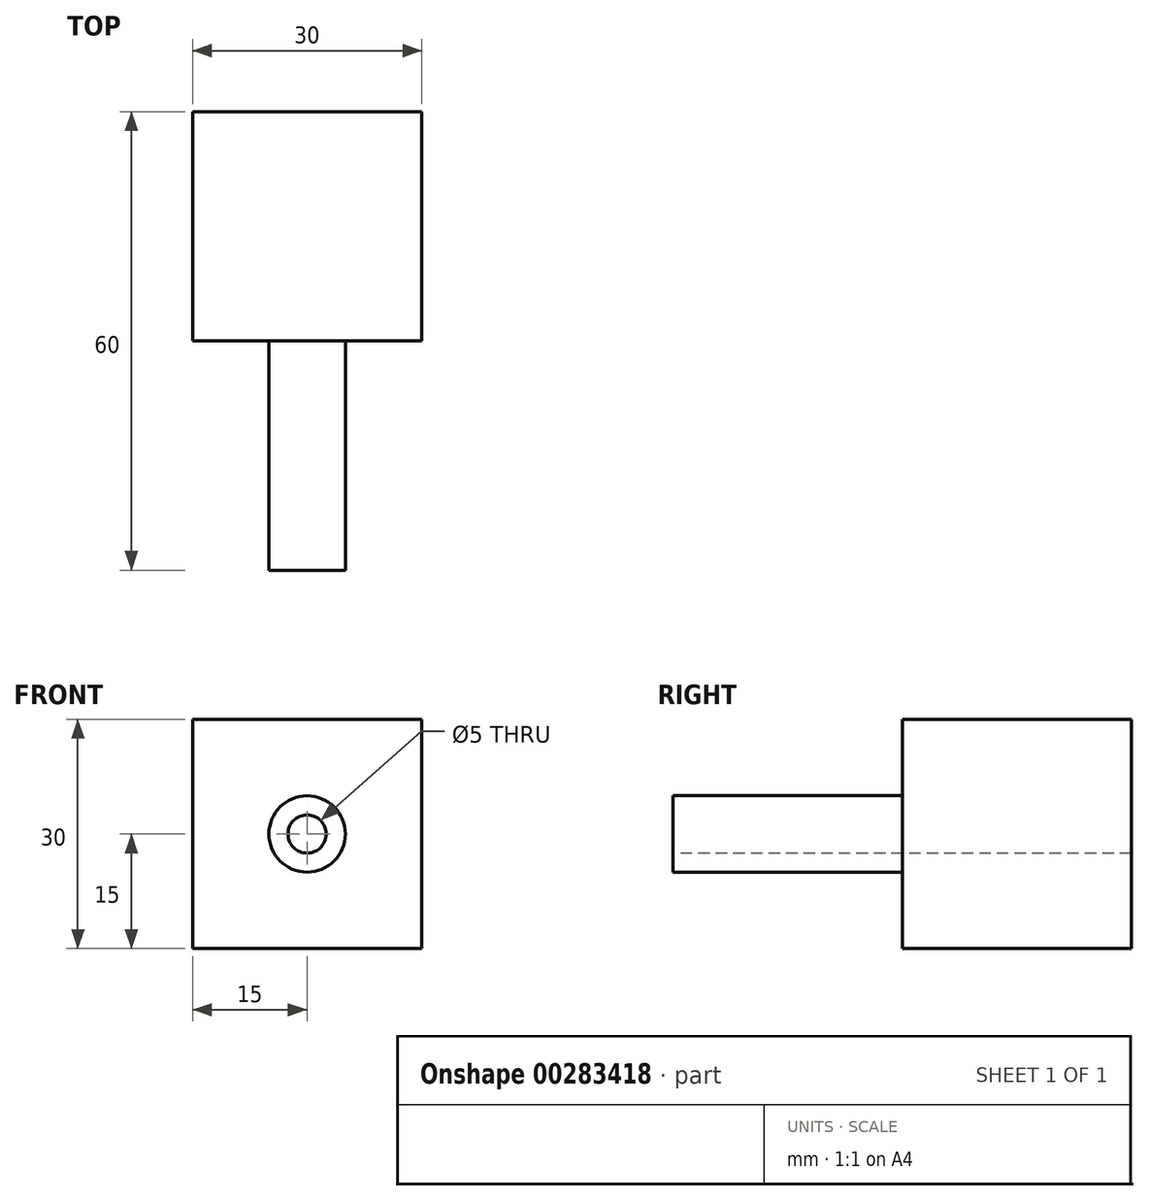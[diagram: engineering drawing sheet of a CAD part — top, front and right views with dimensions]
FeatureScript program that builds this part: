
annotation { "Feature Type Name" : "Feature", "Feature Type Description" : "" }
export const myFeature = defineFeature(function(context is Context, id is Id, definition is map)
    precondition{}
    {
        {
            var Q0;
            Q0=qCreatedBy(makeId("Top.planeOp"),FACE);
            var sketch = newSketch(context, id + "F0", { "sketchPlane" : qUnion([Q0])});
            skLineSegment(sketch, "E0.bottom", {"start": v(-15, 15) * mm, "end": v(15, 15) * mm});
            skLineSegment(sketch, "E0.top", {"start": v(-15, -15) * mm, "end": v(15, -15) * mm});
            skLineSegment(sketch, "E0.left", {"start": v(-15, 15) * mm, "end": v(-15, -15) * mm});
            skLineSegment(sketch, "E0.right", {"start": v(15, 15) * mm, "end": v(15, -15) * mm});
            skPoint(sketch, "E0.middle", {"position": v(0, 0) * mm});
            skSolve(sketch);
        }
        {
            var Q0;
            Q0=makeQuery(id+"F0.imprint","IMPRINT",FACE,{"disambiguationData":[TD([[makeQuery(id+"F0.imprint","IMPRINT",EDGE,{"derivedFrom":sQuery(id+"F0.wireOp",EDGE,"E0.bottom")}),-1.0]])]});
            extrude(context, id + "F1", {"entities" : qUnion([Q0]), "endBound" : BoundingType.SYMMETRIC, "depth" : 30 * mm});
        }
        {
            var Q0;
            Q0=makeQuery(id+"F1.opExtrude","SWEPT_FACE",FACE,{"disambiguationData":[OSD([sQuery(id+"F0.wireOp",EDGE,"E0.top")])]});
            var sketch = newSketch(context, id + "F2", { "sketchPlane" : qUnion([Q0])});
            skCircle(sketch, "E1", {"center": v(0, 0) * mm, "radius": 5 * mm});
            skSolve(sketch);
        }
        {
            var Q0;
            Q0 = qSketchRegion(id + "F2", true);
            extrude(context, id + "F3", {"entities" : qUnion([Q0]), "operationType" : NewBodyOperationType.ADD, "depth" : 30 * mm});
        }
        {
            var Q0;
            Q0=makeQuery(id+"F3.opExtrude","CAP_FACE",FACE,{"disambiguationData":[OSD([sQuery(id+"F2.wireOp",EDGE,"E1")])],"isStart":false});
            var sketch = newSketch(context, id + "F4", { "sketchPlane" : qUnion([Q0])});
            skCircle(sketch, "E2", {"center": v(0, 0) * mm, "radius": 2.5 * mm});
            skSolve(sketch);
        }
        {
            var Q0;
            Q0=makeQuery(id+"F4.imprint","IMPRINT",FACE,{"disambiguationData":[TD([[makeQuery(id+"F4.imprint","IMPRINT",EDGE,{"derivedFrom":sQuery(id+"F4.wireOp",EDGE,"E2")}),1.0]])]});
            var Q1;
            Q1=sQuery(id+"F4.wireOp",EDGE,"E2");
            extrude(context, id + "F5", {"entities" : qUnion([Q0]), "operationType" : NewBodyOperationType.REMOVE, "surfaceEntities" : qUnion([Q1]), "endBound" : BoundingType.THROUGH_ALL, "oppositeDirection" : true, "depth" : 30 * mm});
        }
    });
